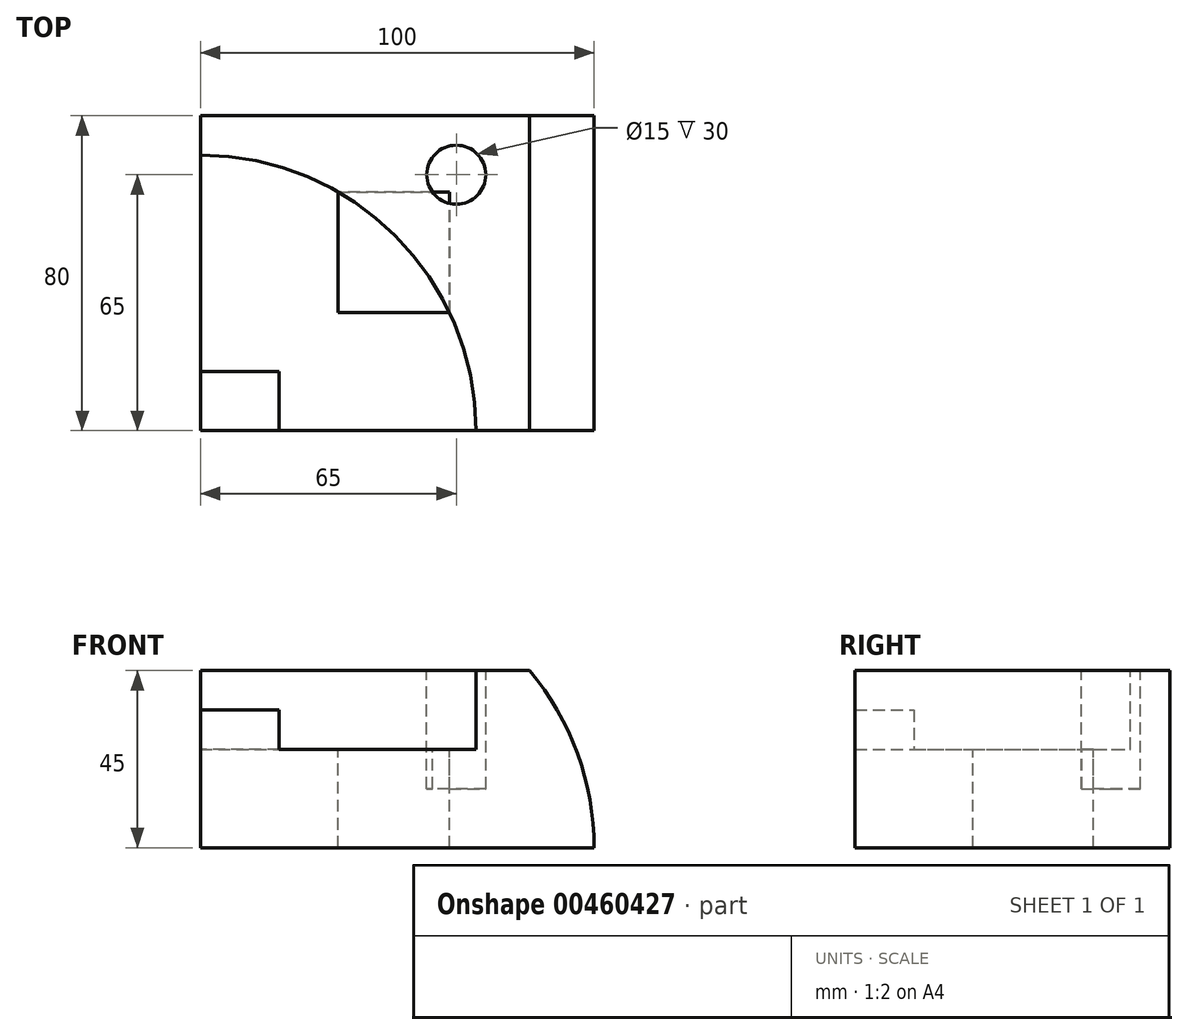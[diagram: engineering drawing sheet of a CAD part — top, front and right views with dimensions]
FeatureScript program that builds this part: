
annotation { "Feature Type Name" : "Feature", "Feature Type Description" : "" }
export const myFeature = defineFeature(function(context is Context, id is Id, definition is map)
    precondition{}
    {
        {
            var Q0;
            Q0=qCreatedBy(makeId("Top.planeOp"),FACE);
            var sketch = newSketch(context, id + "F0", { "sketchPlane" : qUnion([Q0])});
            skLineSegment(sketch, "E0.bottom", {"start": v(0, 0) * mm, "end": v(100, 0) * mm});
            skLineSegment(sketch, "E0.top", {"start": v(0, 80) * mm, "end": v(100, 80) * mm});
            skLineSegment(sketch, "E0.left", {"start": v(0, 0) * mm, "end": v(0, 80) * mm});
            skLineSegment(sketch, "E0.right", {"start": v(100, 0) * mm, "end": v(100, 80) * mm});
            skSolve(sketch);
        }
        {
            var Q0;
            Q0 = qSketchRegion(id + "F0", true);
            extrude(context, id + "F1", {"entities" : qUnion([Q0]), "depth" : 45 * mm});
        }
        {
            var Q0;
            Q0=makeQuery(id+"F1.opExtrude","CAP_FACE",FACE,{"disambiguationData":[OSD([sQuery(id+"F0.wireOp",EDGE,"E0.bottom"),sQuery(id+"F0.wireOp",EDGE,"E0.top"),sQuery(id+"F0.wireOp",EDGE,"E0.left"),sQuery(id+"F0.wireOp",EDGE,"E0.right")])],"isStart":false});
            var sketch = newSketch(context, id + "F2", { "sketchPlane" : qUnion([Q0])});
            skLineSegment(sketch, "E1", {"start": v(0, 80) * mm, "end": v(65, 80) * mm});
            skLineSegment(sketch, "E2", {"start": v(65, 80) * mm, "end": v(65, 65) * mm});
            skCircle(sketch, "E3", {"center": v(65, 65) * mm, "radius": 7.5 * mm});
            skSolve(sketch);
        }
        {
            var Q0;
            Q0=makeQuery(id+"F2.imprint","IMPRINT",FACE,{"disambiguationData":[TD([[makeQuery(id+"F2.imprint","IMPRINT",EDGE,{"derivedFrom":sQuery(id+"F2.wireOp",EDGE,"E3")}),1.0]])]});
            extrude(context, id + "F3", {"entities" : qUnion([Q0]), "operationType" : NewBodyOperationType.REMOVE, "oppositeDirection" : true, "depth" : 30 * mm});
        }
        {
            var Q0;
            Q0=makeQuery(id+"F1.opExtrude","CAP_FACE",FACE,{"disambiguationData":[OSD([sQuery(id+"F0.wireOp",EDGE,"E0.bottom"),sQuery(id+"F0.wireOp",EDGE,"E0.top"),sQuery(id+"F0.wireOp",EDGE,"E0.left"),sQuery(id+"F0.wireOp",EDGE,"E0.right")])],"isStart":false});
            var sketch = newSketch(context, id + "F4", { "sketchPlane" : qUnion([Q0])});
            skCircle(sketch, "E4", {"center": v(0, 0) * mm, "radius": 70 * mm});
            skSolve(sketch);
        }
        {
            var Q0;
            Q0 = qSketchRegion(id + "F4", true);
            extrude(context, id + "F5", {"entities" : qUnion([Q0]), "operationType" : NewBodyOperationType.REMOVE, "oppositeDirection" : true, "depth" : 20 * mm});
        }
        {
            var Q0;
            Q0=makeQuery(id+"F5.boolean.opBoolean","COPY",FACE,{"derivedFrom":makeQuery(id+"F5.opExtrude","CAP_FACE",FACE,{"disambiguationData":[OSD([sQuery(id+"F4.wireOp",EDGE,"E4")])],"isStart":false})});
            var sketch = newSketch(context, id + "F6", { "sketchPlane" : qUnion([Q0])});
            skLineSegment(sketch, "E5.bottom", {"start": v(0, 0) * mm, "end": v(20, 0) * mm});
            skLineSegment(sketch, "E5.top", {"start": v(0, 15) * mm, "end": v(20, 15) * mm});
            skLineSegment(sketch, "E5.left", {"start": v(0, 0) * mm, "end": v(0, 15) * mm});
            skLineSegment(sketch, "E5.right", {"start": v(20, 0) * mm, "end": v(20, 15) * mm});
            skSolve(sketch);
        }
        {
            var Q0;
            Q0 = qSketchRegion(id + "F6", true);
            extrude(context, id + "F7", {"entities" : qUnion([Q0]), "operationType" : NewBodyOperationType.ADD, "depth" : 10 * mm});
        }
        {
            var Q0;
            Q0=makeQuery(id+"F5.boolean.opBoolean","COPY",FACE,{"derivedFrom":makeQuery(id+"F5.opExtrude","CAP_FACE",FACE,{"disambiguationData":[OSD([sQuery(id+"F4.wireOp",EDGE,"E4")])],"isStart":false})});
            var sketch = newSketch(context, id + "F8", { "sketchPlane" : qUnion([Q0])});
            skLineSegment(sketch, "E6", {"start": v(20, 0) * mm, "end": v(35, 0) * mm});
            skLineSegment(sketch, "E7", {"start": v(35, 0) * mm, "end": v(35, 30) * mm});
            skLineSegment(sketch, "E8", {"start": v(35, 30) * mm, "end": v(35, 60.62) * mm});
            skLineSegment(sketch, "E9", {"start": v(35, 30) * mm, "end": v(63.25, 30) * mm});
            skLineSegment(sketch, "E10", {"start": v(63.25, 30) * mm, "end": v(63.25, 60.62) * mm});
            skLineSegment(sketch, "E11", {"start": v(63.25, 60.62) * mm, "end": v(35, 60.62) * mm});
            skSolve(sketch);
        }
        {
            var Q0;
            {var subQ0=sQuery(id+"F8.wireOp",EDGE,"E10");Q0=makeQuery(id+"F8.imprint","IMPRINT",FACE,{"disambiguationData":[TD([[makeQuery(id+"F8.imprint","IMPRINT",EDGE,{"derivedFrom":subQ0}),1.0]])]});}
            var Q1;
            {var subQ0=sQuery(id+"F8.wireOp",EDGE,"E8");Q1=makeQuery(id+"F8.imprint","IMPRINT",FACE,{"disambiguationData":[TD([[makeQuery(id+"F8.imprint","IMPRINT",EDGE,{"derivedFrom":subQ0}),-1.0]])]});}
            extrude(context, id + "F9", {"entities" : qUnion([Q0, Q1]), "operationType" : NewBodyOperationType.REMOVE, "endBound" : BoundingType.UP_TO_NEXT, "oppositeDirection" : true, "depth" : 25 * mm});
        }
        {
            var Q0;
            Q0=makeQuery(id+"F7.boolean.opBoolean","MERGE",FACE,{"derivedFrom":[makeQuery(id+"F1.opExtrude","SWEPT_FACE",FACE,{"disambiguationData":[OSD([sQuery(id+"F0.wireOp",EDGE,"E0.bottom")])]}),makeQuery(id+"F7.opExtrude","SWEPT_FACE",FACE,{"disambiguationData":[OSD([sQuery(id+"F6.wireOp",EDGE,"E5.bottom")])]})]});
            var sketch = newSketch(context, id + "F10", { "sketchPlane" : qUnion([Q0])});
            skLineSegment(sketch, "E12", {"start": v(0, 0) * mm, "end": v(30, 0) * mm});
            skCircle(sketch, "E13", {"center": v(30, 0) * mm, "radius": 70 * mm});
            skSolve(sketch);
        }
        {
            var Q0;
            {var subQ1=sQuery(id+"F0.wireOp",EDGE,"E0.bottom");var subQ2=makeQuery(id+"F1.opExtrude","SWEPT_EDGE",EDGE,{"disambiguationData":[OSD([subQ1,sQuery(id+"F0.wireOp",EDGE,"E0.right")])]});Q0=makeQuery(id+"F10.imprint","IMPRINT",FACE,{"disambiguationData":[TD([[makeQuery(id+"F10.imprint","IMPRINT",EDGE,{"derivedFrom":subQ2}),-1.0]])]});}
            extrude(context, id + "F11", {"entities" : qUnion([Q0]), "operationType" : NewBodyOperationType.REMOVE, "endBound" : BoundingType.UP_TO_NEXT, "oppositeDirection" : true, "depth" : 25 * mm});
        }
    });
